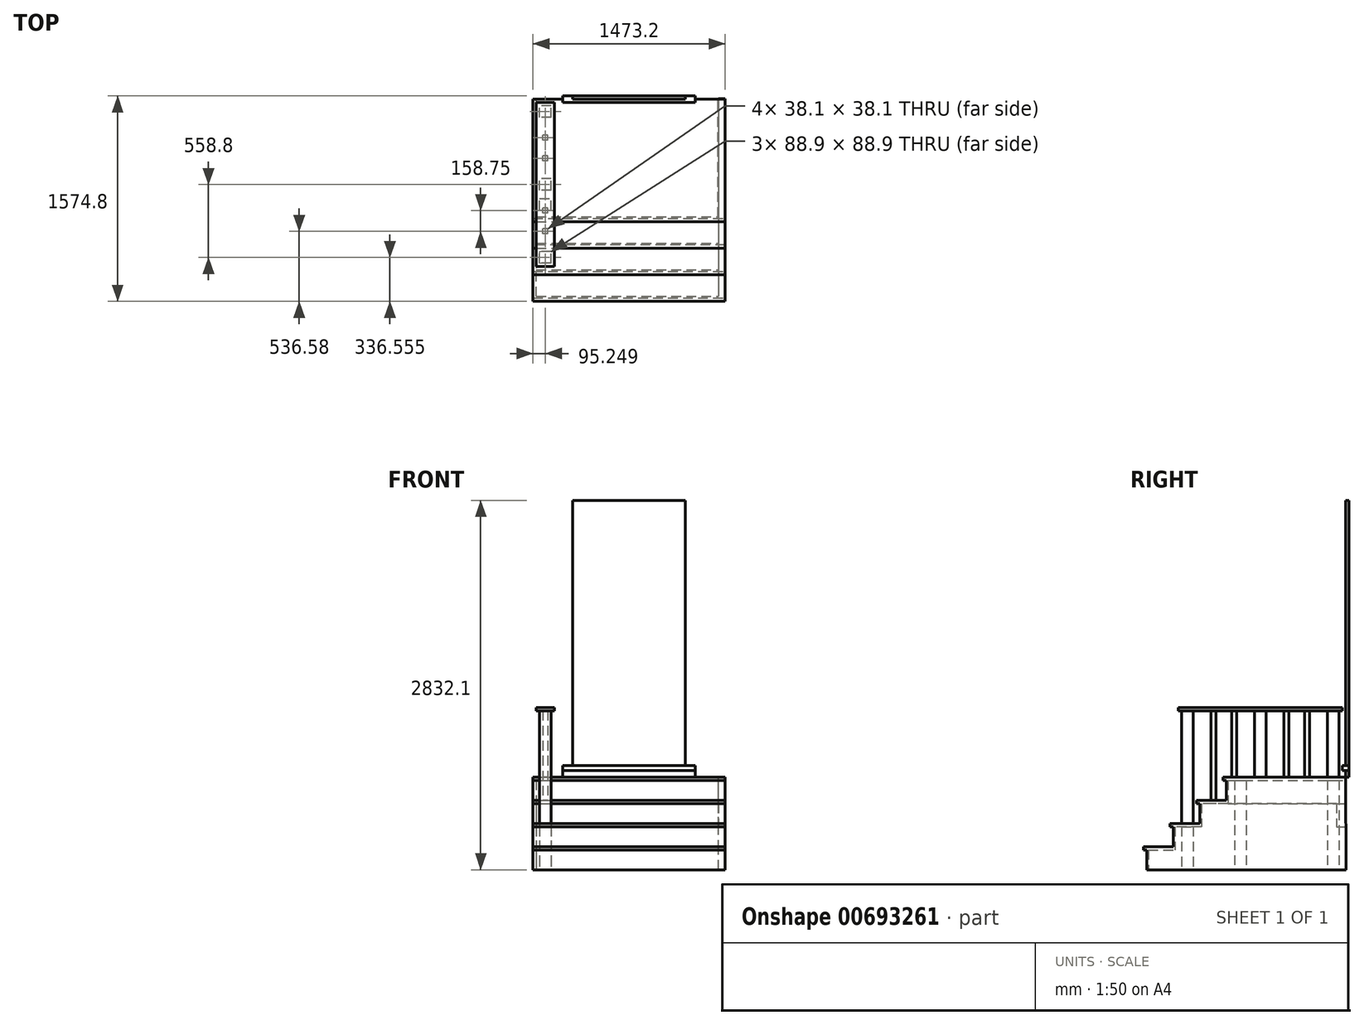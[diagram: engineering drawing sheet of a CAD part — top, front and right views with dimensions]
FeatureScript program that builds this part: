
annotation { "Feature Type Name" : "Feature", "Feature Type Description" : "" }
export const myFeature = defineFeature(function(context is Context, id is Id, definition is map)
    precondition{}
    {
        {
            var Q0;
            Q0=qCreatedBy(makeId("Top.planeOp"),FACE);
            var sketch = newSketch(context, id + "F0", { "sketchPlane" : qUnion([Q0])});
            skLineSegment(sketch, "E0", {"start": v(-1026.48, 307.92) * mm, "end": v(802.32, 307.92) * mm});
            skLineSegment(sketch, "E1", {"start": v(802.32, 307.92) * mm, "end": v(802.32, -200.08) * mm});
            skLineSegment(sketch, "E2", {"start": v(802.32, -200.08) * mm, "end": v(395.92, -606.48) * mm});
            skLineSegment(sketch, "E3", {"start": v(395.92, -606.48) * mm, "end": v(-1026.48, -606.48) * mm});
            skLineSegment(sketch, "E4", {"start": v(-1026.48, -606.48) * mm, "end": v(-1026.48, 307.92) * mm});
            skSolve(sketch);
        }
        {
            var Q0;
            Q0 = qSketchRegion(id + "F0", true);
            extrude(context, id + "F1", {"entities" : qUnion([Q0]), "depth" : 711.2 * mm, "offsetDistance" : 25.4 * mm});
        }
        {
            var Q0;
            Q0=qCreatedBy(makeId("Top.planeOp"),FACE);
            var sketch = newSketch(context, id + "F2", { "sketchPlane" : qUnion([Q0])});
            skLineSegment(sketch, "E5", {"start": v(-1026.48, -606.48) * mm, "end": v(-1026.48, -809.68) * mm});
            skLineSegment(sketch, "E6", {"start": v(-1026.48, -809.68) * mm, "end": v(480.09, -809.68) * mm});
            skLineSegment(sketch, "E7", {"start": v(480.09, -809.68) * mm, "end": v(1005.52, -284.24) * mm});
            skLineSegment(sketch, "E8", {"start": v(1005.52, -284.24) * mm, "end": v(1005.52, 307.92) * mm});
            skLineSegment(sketch, "E9", {"start": v(1005.52, 307.92) * mm, "end": v(802.32, 307.92) * mm});
            skLineSegment(sketch, "E10", {"start": v(-1026.48, -606.48) * mm, "end": v(395.92, -606.48) * mm});
            skLineSegment(sketch, "E11", {"start": v(395.92, -606.48) * mm, "end": v(802.32, -200.08) * mm});
            skLineSegment(sketch, "E12", {"start": v(802.32, -200.08) * mm, "end": v(802.32, 307.92) * mm});
            skSolve(sketch);
        }
        {
            var Q0;
            Q0 = qSketchRegion(id + "F2", true);
            extrude(context, id + "F3", {"entities" : qUnion([Q0]), "operationType" : NewBodyOperationType.ADD, "depth" : 533.4 * mm, "offsetDistance" : 25.4 * mm});
        }
        {
            var Q0;
            Q0=qCreatedBy(makeId("Top.planeOp"),FACE);
            var sketch = newSketch(context, id + "F4", { "sketchPlane" : qUnion([Q0])});
            skLineSegment(sketch, "E13", {"start": v(-1026.48, -809.68) * mm, "end": v(-1026.48, -1012.88) * mm});
            skLineSegment(sketch, "E14", {"start": v(-1026.48, -1012.88) * mm, "end": v(564.26, -1012.88) * mm});
            skLineSegment(sketch, "E15", {"start": v(564.26, -1012.88) * mm, "end": v(1208.72, -368.41) * mm});
            skLineSegment(sketch, "E16", {"start": v(1208.72, -368.41) * mm, "end": v(1208.72, 307.92) * mm});
            skLineSegment(sketch, "E17", {"start": v(1208.72, 307.92) * mm, "end": v(1005.52, 307.92) * mm});
            skLineSegment(sketch, "E18", {"start": v(1005.52, 307.92) * mm, "end": v(1005.52, -284.24) * mm});
            skLineSegment(sketch, "E19", {"start": v(1005.52, -284.24) * mm, "end": v(480.09, -809.68) * mm});
            skLineSegment(sketch, "E20", {"start": v(480.09, -809.68) * mm, "end": v(-1026.48, -809.68) * mm});
            skSolve(sketch);
        }
        {
            var Q0;
            Q0 = qSketchRegion(id + "F4", true);
            extrude(context, id + "F5", {"entities" : qUnion([Q0]), "operationType" : NewBodyOperationType.ADD, "depth" : 355.6 * mm, "offsetDistance" : 25.4 * mm});
        }
        {
            var Q0;
            Q0=qCreatedBy(makeId("Top.planeOp"),FACE);
            var sketch = newSketch(context, id + "F6", { "sketchPlane" : qUnion([Q0])});
            skLineSegment(sketch, "E21", {"start": v(-1026.48, -1012.88) * mm, "end": v(-1026.48, -1216.08) * mm});
            skLineSegment(sketch, "E22", {"start": v(-1026.48, -1216.08) * mm, "end": v(648.42, -1216.08) * mm});
            skLineSegment(sketch, "E23", {"start": v(648.42, -1216.08) * mm, "end": v(1411.92, -452.58) * mm});
            skLineSegment(sketch, "E24", {"start": v(1411.92, -452.58) * mm, "end": v(1411.92, 307.92) * mm});
            skLineSegment(sketch, "E25", {"start": v(1411.92, 307.92) * mm, "end": v(1208.72, 307.92) * mm});
            skLineSegment(sketch, "E26", {"start": v(-1026.48, -1012.88) * mm, "end": v(564.26, -1012.88) * mm});
            skLineSegment(sketch, "E27", {"start": v(564.26, -1012.88) * mm, "end": v(1208.72, -368.41) * mm});
            skLineSegment(sketch, "E28", {"start": v(1208.72, -368.41) * mm, "end": v(1208.72, 307.92) * mm});
            skSolve(sketch);
        }
        {
            var Q0;
            Q0 = qSketchRegion(id + "F6", true);
            extrude(context, id + "F7", {"entities" : qUnion([Q0]), "operationType" : NewBodyOperationType.ADD, "depth" : 177.8 * mm, "offsetDistance" : 25.4 * mm});
        }
        {
            var Q0;
            Q0=qCreatedBy(makeId("Top.planeOp"),FACE);
            var sketch = newSketch(context, id + "F8", { "sketchPlane" : qUnion([Q0])});
            skLineSegment(sketch, "E29.bottom", {"start": v(-975.68, -860.48) * mm, "end": v(-886.78, -860.48) * mm});
            skLineSegment(sketch, "E29.top", {"start": v(-975.68, -949.38) * mm, "end": v(-886.78, -949.38) * mm});
            skLineSegment(sketch, "E29.left", {"start": v(-975.68, -860.48) * mm, "end": v(-975.68, -949.38) * mm});
            skLineSegment(sketch, "E29.right", {"start": v(-886.78, -860.48) * mm, "end": v(-886.78, -949.38) * mm});
            skPoint(sketch, "E30.oppositeSnap0", {"position": v(-886.78, -904.93) * mm});
            skLineSegment(sketch, "E30.bottom", {"start": v(-975.68, 257.12) * mm, "end": v(-886.78, 257.12) * mm});
            skLineSegment(sketch, "E30.top", {"start": v(-975.68, 168.22) * mm, "end": v(-886.78, 168.22) * mm});
            skLineSegment(sketch, "E30.left", {"start": v(-975.68, 257.12) * mm, "end": v(-975.68, 168.22) * mm});
            skLineSegment(sketch, "E30.right", {"start": v(-886.78, 257.12) * mm, "end": v(-886.78, 168.22) * mm});
            skLineSegment(sketch, "E31.bottom", {"start": v(-975.68, -301.68) * mm, "end": v(-886.78, -301.68) * mm});
            skLineSegment(sketch, "E31.top", {"start": v(-975.68, -390.58) * mm, "end": v(-886.78, -390.58) * mm});
            skLineSegment(sketch, "E31.left", {"start": v(-975.68, -301.68) * mm, "end": v(-975.68, -390.58) * mm});
            skLineSegment(sketch, "E31.right", {"start": v(-886.78, -301.68) * mm, "end": v(-886.78, -390.58) * mm});
            skLineSegment(sketch, "E32.bottom", {"start": v(-950.28, 31.7) * mm, "end": v(-912.18, 31.7) * mm});
            skLineSegment(sketch, "E32.top", {"start": v(-950.28, -6.4) * mm, "end": v(-912.18, -6.4) * mm});
            skLineSegment(sketch, "E32.left", {"start": v(-950.28, 31.7) * mm, "end": v(-950.28, -6.4) * mm});
            skLineSegment(sketch, "E32.right", {"start": v(-912.18, 31.7) * mm, "end": v(-912.18, -6.4) * mm});
            skLineSegment(sketch, "E33.bottom", {"start": v(-950.28, -127.05) * mm, "end": v(-912.18, -127.05) * mm});
            skLineSegment(sketch, "E33.top", {"start": v(-950.28, -165.15) * mm, "end": v(-912.18, -165.15) * mm});
            skLineSegment(sketch, "E33.left", {"start": v(-950.28, -127.05) * mm, "end": v(-950.28, -165.15) * mm});
            skLineSegment(sketch, "E33.right", {"start": v(-912.18, -127.05) * mm, "end": v(-912.18, -165.15) * mm});
            skLineSegment(sketch, "E34.bottom", {"start": v(-950.28, -527.1) * mm, "end": v(-912.18, -527.1) * mm});
            skLineSegment(sketch, "E34.top", {"start": v(-950.28, -565.2) * mm, "end": v(-912.18, -565.2) * mm});
            skLineSegment(sketch, "E34.left", {"start": v(-950.28, -527.1) * mm, "end": v(-950.28, -565.2) * mm});
            skLineSegment(sketch, "E34.right", {"start": v(-912.18, -527.1) * mm, "end": v(-912.18, -565.2) * mm});
            skLineSegment(sketch, "E35.bottom", {"start": v(-950.28, -685.85) * mm, "end": v(-912.18, -685.85) * mm});
            skLineSegment(sketch, "E35.top", {"start": v(-950.28, -723.95) * mm, "end": v(-912.18, -723.95) * mm});
            skLineSegment(sketch, "E35.left", {"start": v(-950.28, -685.85) * mm, "end": v(-950.28, -723.95) * mm});
            skLineSegment(sketch, "E35.right", {"start": v(-912.18, -685.85) * mm, "end": v(-912.18, -723.95) * mm});
            skSolve(sketch);
        }
        {
            var Q0;
            Q0 = qSketchRegion(id + "F8", true);
            extrude(context, id + "F9", {"entities" : qUnion([Q0]), "operationType" : NewBodyOperationType.ADD, "depth" : 1219.2 * mm, "offsetDistance" : 25.4 * mm});
        }
        {
            var Q0;
            Q0=makeQuery(id+"F9.opExtrude","CAP_FACE",FACE,{"disambiguationData":[OSD([sQuery(id+"F8.wireOp",EDGE,"E30.bottom"),sQuery(id+"F8.wireOp",EDGE,"E30.top"),sQuery(id+"F8.wireOp",EDGE,"E30.left"),sQuery(id+"F8.wireOp",EDGE,"E30.right")])],"isStart":false});
            var sketch = newSketch(context, id + "F10", { "sketchPlane" : qUnion([Q0])});
            skLineSegment(sketch, "E36.bottom", {"start": v(-1000.99, 282.52) * mm, "end": v(-861.29, 282.52) * mm});
            skLineSegment(sketch, "E36.top", {"start": v(-1000.99, -974.78) * mm, "end": v(-861.29, -974.78) * mm});
            skLineSegment(sketch, "E36.left", {"start": v(-1000.99, 282.52) * mm, "end": v(-1000.99, -974.78) * mm});
            skLineSegment(sketch, "E36.right", {"start": v(-861.29, 282.52) * mm, "end": v(-861.29, -974.78) * mm});
            skSolve(sketch);
        }
        {
            var Q0;
            Q0 = qSketchRegion(id + "F10", true);
            extrude(context, id + "F11", {"entities" : qUnion([Q0]), "operationType" : NewBodyOperationType.ADD, "depth" : 25.4 * mm, "offsetDistance" : 25.4 * mm});
        }
        {
            var Q0;
            Q0=makeQuery(id+"F7.boolean.opBoolean","MERGE",FACE,{"derivedFrom":[makeQuery(id+"F5.boolean.opBoolean","MERGE",FACE,{"derivedFrom":[makeQuery(id+"F3.boolean.opBoolean","MERGE",FACE,{"derivedFrom":[makeQuery(id+"F1.opExtrude","SWEPT_FACE",FACE,{"disambiguationData":[OSD([sQuery(id+"F0.wireOp",EDGE,"E0")])]}),makeQuery(id+"F3.opExtrude","SWEPT_FACE",FACE,{"disambiguationData":[OSD([sQuery(id+"F2.wireOp",EDGE,"E9")])]})]}),makeQuery(id+"F5.opExtrude","SWEPT_FACE",FACE,{"disambiguationData":[OSD([sQuery(id+"F4.wireOp",EDGE,"E17")])]})]}),makeQuery(id+"F7.opExtrude","SWEPT_FACE",FACE,{"disambiguationData":[OSD([sQuery(id+"F6.wireOp",EDGE,"E25")])]})]});
            var sketch = newSketch(context, id + "F12", { "sketchPlane" : qUnion([Q0])});
            skLineSegment(sketch, "E37.bottom", {"start": v(-141.92, 800.1) * mm, "end": v(721.68, 800.1) * mm});
            skLineSegment(sketch, "E37.top", {"start": v(-141.92, 2832.1) * mm, "end": v(721.68, 2832.1) * mm});
            skLineSegment(sketch, "E37.left", {"start": v(-141.92, 800.1) * mm, "end": v(-141.92, 2832.1) * mm});
            skLineSegment(sketch, "E37.right", {"start": v(721.68, 800.1) * mm, "end": v(721.68, 2832.1) * mm});
            skSolve(sketch);
        }
        {
            var Q0;
            Q0 = qSketchRegion(id + "F12", true);
            extrude(context, id + "F13", {"entities" : qUnion([Q0]), "depth" : 25.4 * mm, "offsetDistance" : 25.4 * mm});
        }
        {
            var Q0;
            Q0=makeQuery(id+"F7.boolean.opBoolean","MERGE",FACE,{"derivedFrom":[makeQuery(id+"F5.boolean.opBoolean","MERGE",FACE,{"derivedFrom":[makeQuery(id+"F3.boolean.opBoolean","MERGE",FACE,{"derivedFrom":[makeQuery(id+"F1.opExtrude","SWEPT_FACE",FACE,{"disambiguationData":[OSD([sQuery(id+"F0.wireOp",EDGE,"E0")])]}),makeQuery(id+"F3.opExtrude","SWEPT_FACE",FACE,{"disambiguationData":[OSD([sQuery(id+"F2.wireOp",EDGE,"E9")])]})]}),makeQuery(id+"F5.opExtrude","SWEPT_FACE",FACE,{"disambiguationData":[OSD([sQuery(id+"F4.wireOp",EDGE,"E17")])]})]}),makeQuery(id+"F7.opExtrude","SWEPT_FACE",FACE,{"disambiguationData":[OSD([sQuery(id+"F6.wireOp",EDGE,"E25")])]})]});
            var sketch = newSketch(context, id + "F14", { "sketchPlane" : qUnion([Q0])});
            skLineSegment(sketch, "E38.bottom", {"start": v(-218.12, 800.1) * mm, "end": v(797.88, 800.1) * mm});
            skLineSegment(sketch, "E38.top", {"start": v(-218.12, 762) * mm, "end": v(797.88, 762) * mm});
            skLineSegment(sketch, "E38.left", {"start": v(-218.12, 800.1) * mm, "end": v(-218.12, 762) * mm});
            skLineSegment(sketch, "E38.right", {"start": v(797.88, 800.1) * mm, "end": v(797.88, 762) * mm});
            skSolve(sketch);
        }
        {
            var Q0;
            Q0 = qSketchRegion(id + "F14", true);
            extrude(context, id + "F15", {"entities" : qUnion([Q0]), "depth" : 25.4 * mm, "offsetDistance" : 25.4 * mm, "hasSecondDirection" : true, "secondDirectionOppositeDirection" : true, "secondDirectionDepth" : 25.4 * mm});
        }
        {
            var Q0;
            Q0=makeQuery(id+"F7.boolean.opBoolean","MERGE",FACE,{"derivedFrom":[makeQuery(id+"F5.boolean.opBoolean","MERGE",FACE,{"derivedFrom":[makeQuery(id+"F3.boolean.opBoolean","MERGE",FACE,{"derivedFrom":[makeQuery(id+"F1.opExtrude","SWEPT_FACE",FACE,{"disambiguationData":[OSD([sQuery(id+"F0.wireOp",EDGE,"E0")])]}),makeQuery(id+"F3.opExtrude","SWEPT_FACE",FACE,{"disambiguationData":[OSD([sQuery(id+"F2.wireOp",EDGE,"E9")])]})]}),makeQuery(id+"F5.opExtrude","SWEPT_FACE",FACE,{"disambiguationData":[OSD([sQuery(id+"F4.wireOp",EDGE,"E17")])]})]}),makeQuery(id+"F7.opExtrude","SWEPT_FACE",FACE,{"disambiguationData":[OSD([sQuery(id+"F6.wireOp",EDGE,"E25")])]})]});
            var sketch = newSketch(context, id + "F16", { "sketchPlane" : qUnion([Q0])});
            skLineSegment(sketch, "E39.bottom", {"start": v(-218.12, 762) * mm, "end": v(797.88, 762) * mm});
            skLineSegment(sketch, "E39.top", {"start": v(-218.12, 711.2) * mm, "end": v(797.88, 711.2) * mm});
            skLineSegment(sketch, "E39.left", {"start": v(-218.12, 762) * mm, "end": v(-218.12, 711.2) * mm});
            skLineSegment(sketch, "E39.right", {"start": v(797.88, 762) * mm, "end": v(797.88, 711.2) * mm});
            skSolve(sketch);
        }
        {
            var Q0;
            Q0 = qSketchRegion(id + "F16", true);
            extrude(context, id + "F17", {"entities" : qUnion([Q0]), "depth" : 25.4 * mm, "offsetDistance" : 25.4 * mm});
        }
        {
            var Q0;
            Q0=makeQuery(id+"F1.opExtrude","CAP_FACE",FACE,{"disambiguationData":[OSD([sQuery(id+"F0.wireOp",EDGE,"E0"),sQuery(id+"F0.wireOp",EDGE,"E1"),sQuery(id+"F0.wireOp",EDGE,"E2"),sQuery(id+"F0.wireOp",EDGE,"E3"),sQuery(id+"F0.wireOp",EDGE,"E4")])],"isStart":false});
            var sketch = newSketch(context, id + "F18", { "sketchPlane" : qUnion([Q0])});
            skLineSegment(sketch, "E40", {"start": v(-1026.48, -606.48) * mm, "end": v(-1026.48, -631.88) * mm});
            skLineSegment(sketch, "E41", {"start": v(-1026.48, -631.88) * mm, "end": v(406.44, -631.88) * mm});
            skLineSegment(sketch, "E42", {"start": v(406.44, -631.88) * mm, "end": v(827.72, -210.6) * mm});
            skLineSegment(sketch, "E43", {"start": v(827.72, -210.6) * mm, "end": v(827.72, 307.92) * mm});
            skLineSegment(sketch, "E44", {"start": v(827.72, 307.92) * mm, "end": v(802.32, 307.92) * mm});
            skLineSegment(sketch, "E45", {"start": v(802.32, 307.92) * mm, "end": v(802.32, -200.08) * mm});
            skLineSegment(sketch, "E46", {"start": v(802.32, -200.08) * mm, "end": v(395.92, -606.48) * mm});
            skLineSegment(sketch, "E47", {"start": v(395.92, -606.48) * mm, "end": v(-1026.48, -606.48) * mm});
            skSolve(sketch);
        }
        {
            var Q0;
            Q0 = qSketchRegion(id + "F18", true);
            var Q1;
            Q1=makeQuery(id+"F18.imprint","IMPRINT",FACE,{"disambiguationData":[TD([[makeQuery(id+"F18.imprint","IMPRINT",EDGE,{"derivedFrom":sQuery(id+"F18.wireOp",EDGE,"E45")}),-1.0]])]});
            extrude(context, id + "F19", {"entities" : qUnion([Q0, Q1]), "operationType" : NewBodyOperationType.ADD, "oppositeDirection" : true, "depth" : 25.4 * mm, "offsetDistance" : 25.4 * mm});
        }
        {
            var Q0;
            Q0=makeQuery(id+"F3.opExtrude","CAP_FACE",FACE,{"disambiguationData":[OSD([sQuery(id+"F2.wireOp",EDGE,"E5"),sQuery(id+"F2.wireOp",EDGE,"E6"),sQuery(id+"F2.wireOp",EDGE,"E7"),sQuery(id+"F2.wireOp",EDGE,"E8"),sQuery(id+"F2.wireOp",EDGE,"E9"),sQuery(id+"F2.wireOp",EDGE,"E10"),sQuery(id+"F2.wireOp",EDGE,"E11"),sQuery(id+"F2.wireOp",EDGE,"E12")])],"isStart":false});
            var sketch = newSketch(context, id + "F20", { "sketchPlane" : qUnion([Q0])});
            skLineSegment(sketch, "E48", {"start": v(-1026.48, -809.68) * mm, "end": v(-1026.48, -835.08) * mm});
            skLineSegment(sketch, "E49", {"start": v(-1026.48, -835.08) * mm, "end": v(490.6, -835.08) * mm});
            skLineSegment(sketch, "E50", {"start": v(490.6, -835.08) * mm, "end": v(1030.92, -294.76) * mm});
            skLineSegment(sketch, "E51", {"start": v(1030.92, -294.76) * mm, "end": v(1030.92, 308.43) * mm});
            skLineSegment(sketch, "E52", {"start": v(1030.92, 308.43) * mm, "end": v(1005.52, 307.92) * mm});
            skLineSegment(sketch, "E53", {"start": v(1005.52, 307.92) * mm, "end": v(1005.52, -284.24) * mm});
            skLineSegment(sketch, "E54", {"start": v(1005.52, -284.24) * mm, "end": v(480.09, -809.68) * mm});
            skLineSegment(sketch, "E55", {"start": v(480.09, -809.68) * mm, "end": v(-1026.48, -809.68) * mm});
            skSolve(sketch);
        }
        {
            var Q0;
            Q0 = qSketchRegion(id + "F20", true);
            extrude(context, id + "F21", {"entities" : qUnion([Q0]), "operationType" : NewBodyOperationType.ADD, "oppositeDirection" : true, "depth" : 25.4 * mm, "offsetDistance" : 25.4 * mm});
        }
        {
            var Q0;
            Q0=makeQuery(id+"F5.opExtrude","CAP_FACE",FACE,{"disambiguationData":[OSD([sQuery(id+"F4.wireOp",EDGE,"E13"),sQuery(id+"F4.wireOp",EDGE,"E14"),sQuery(id+"F4.wireOp",EDGE,"E15"),sQuery(id+"F4.wireOp",EDGE,"E16"),sQuery(id+"F4.wireOp",EDGE,"E17"),sQuery(id+"F4.wireOp",EDGE,"E18"),sQuery(id+"F4.wireOp",EDGE,"E19"),sQuery(id+"F4.wireOp",EDGE,"E20")])],"isStart":false});
            var sketch = newSketch(context, id + "F22", { "sketchPlane" : qUnion([Q0])});
            skLineSegment(sketch, "E56", {"start": v(-1026.48, -1012.88) * mm, "end": v(-1026.48, -1038.28) * mm});
            skLineSegment(sketch, "E57", {"start": v(-1026.48, -1038.28) * mm, "end": v(574.78, -1038.28) * mm});
            skLineSegment(sketch, "E58", {"start": v(574.78, -1038.28) * mm, "end": v(1234.12, -378.93) * mm});
            skLineSegment(sketch, "E59", {"start": v(1234.12, -378.93) * mm, "end": v(1234.12, 307.92) * mm});
            skLineSegment(sketch, "E60", {"start": v(1234.12, 307.92) * mm, "end": v(1208.72, 307.92) * mm});
            skLineSegment(sketch, "E61", {"start": v(1208.72, 307.92) * mm, "end": v(1208.72, -368.41) * mm});
            skLineSegment(sketch, "E62", {"start": v(1208.72, -368.41) * mm, "end": v(564.26, -1012.88) * mm});
            skLineSegment(sketch, "E63", {"start": v(564.26, -1012.88) * mm, "end": v(-1026.48, -1012.88) * mm});
            skSolve(sketch);
        }
        {
            var Q0;
            Q0 = qSketchRegion(id + "F22", true);
            extrude(context, id + "F23", {"entities" : qUnion([Q0]), "operationType" : NewBodyOperationType.ADD, "oppositeDirection" : true, "depth" : 25.4 * mm, "offsetDistance" : 25.4 * mm});
        }
        {
            var Q0;
            Q0=makeQuery(id+"F7.opExtrude","CAP_FACE",FACE,{"disambiguationData":[OSD([sQuery(id+"F6.wireOp",EDGE,"E21"),sQuery(id+"F6.wireOp",EDGE,"E22"),sQuery(id+"F6.wireOp",EDGE,"E23"),sQuery(id+"F6.wireOp",EDGE,"E24"),sQuery(id+"F6.wireOp",EDGE,"E25"),sQuery(id+"F6.wireOp",EDGE,"E26"),sQuery(id+"F6.wireOp",EDGE,"E27"),sQuery(id+"F6.wireOp",EDGE,"E28")])],"isStart":false});
            var sketch = newSketch(context, id + "F24", { "sketchPlane" : qUnion([Q0])});
            skLineSegment(sketch, "E64", {"start": v(-1026.48, -1216.08) * mm, "end": v(-1026.48, -1241.48) * mm});
            skLineSegment(sketch, "E65", {"start": v(-1026.48, -1241.48) * mm, "end": v(658.95, -1241.48) * mm});
            skLineSegment(sketch, "E66", {"start": v(658.95, -1241.48) * mm, "end": v(1439.04, -461.38) * mm});
            skLineSegment(sketch, "E67", {"start": v(1439.04, -461.38) * mm, "end": v(1437.32, 307.92) * mm});
            skLineSegment(sketch, "E68", {"start": v(1437.32, 307.92) * mm, "end": v(1411.92, 307.92) * mm});
            skLineSegment(sketch, "E69", {"start": v(1411.92, 307.92) * mm, "end": v(1411.92, -452.58) * mm});
            skLineSegment(sketch, "E70", {"start": v(1411.92, -452.58) * mm, "end": v(648.42, -1216.08) * mm});
            skLineSegment(sketch, "E71", {"start": v(648.42, -1216.08) * mm, "end": v(-1026.48, -1216.08) * mm});
            skSolve(sketch);
        }
        {
            var Q0;
            Q0 = qSketchRegion(id + "F24", true);
            extrude(context, id + "F25", {"entities" : qUnion([Q0]), "operationType" : NewBodyOperationType.ADD, "oppositeDirection" : true, "depth" : 25.4 * mm, "offsetDistance" : 25.4 * mm});
        }
        {
            var Q0;
            {var subQ0=sQuery(id+"F0.wireOp",EDGE,"E4");var subQ1=sQuery(id+"F0.wireOp",EDGE,"E3");var subQ2=sQuery(id+"F0.wireOp",EDGE,"E2");var subQ3=sQuery(id+"F0.wireOp",EDGE,"E1");var subQ4=sQuery(id+"F0.wireOp",EDGE,"E0");Q0=makeQuery(id+"F19.boolean.opBoolean","MERGE",FACE,{"derivedFrom":[makeQuery(id+"F1.opExtrude","CAP_FACE",FACE,{"disambiguationData":[OSD([subQ4,subQ3,subQ2,subQ1,subQ0])],"isStart":false}),makeQuery(id+"F19.opExtrude","CAP_FACE",FACE,{"disambiguationData":[OSD([subQ4,subQ3,subQ2,subQ1,subQ0,sQuery(id+"F8.wireOp",EDGE,"E30.bottom"),sQuery(id+"F8.wireOp",EDGE,"E30.top"),sQuery(id+"F8.wireOp",EDGE,"E30.left"),sQuery(id+"F8.wireOp",EDGE,"E30.right"),sQuery(id+"F8.wireOp",EDGE,"E31.bottom"),sQuery(id+"F8.wireOp",EDGE,"E31.top"),sQuery(id+"F8.wireOp",EDGE,"E31.left"),sQuery(id+"F8.wireOp",EDGE,"E31.right"),sQuery(id+"F8.wireOp",EDGE,"E32.bottom"),sQuery(id+"F8.wireOp",EDGE,"E32.top"),sQuery(id+"F8.wireOp",EDGE,"E32.left"),sQuery(id+"F8.wireOp",EDGE,"E32.right"),sQuery(id+"F8.wireOp",EDGE,"E33.bottom"),sQuery(id+"F8.wireOp",EDGE,"E33.top"),sQuery(id+"F8.wireOp",EDGE,"E33.left"),sQuery(id+"F8.wireOp",EDGE,"E33.right"),sQuery(id+"F8.wireOp",EDGE,"E34.bottom"),sQuery(id+"F8.wireOp",EDGE,"E34.top"),sQuery(id+"F8.wireOp",EDGE,"E34.left"),sQuery(id+"F8.wireOp",EDGE,"E34.right"),sQuery(id+"F18.wireOp",EDGE,"E40"),sQuery(id+"F18.wireOp",EDGE,"E41"),sQuery(id+"F18.wireOp",EDGE,"E42"),sQuery(id+"F18.wireOp",EDGE,"E43"),sQuery(id+"F18.wireOp",EDGE,"E44")])],"isStart":true})]});}
            var sketch = newSketch(context, id + "F26", { "sketchPlane" : qUnion([Q0])});
            skLineSegment(sketch, "E72.bottom", {"start": v(-1026.48, 206.32) * mm, "end": v(446.72, 206.32) * mm});
            skLineSegment(sketch, "E73", {"start": v(-1026.48, -492.18) * mm, "end": v(458.58, -492.18) * mm});
            skLineSegment(sketch, "E74", {"start": v(-1026.48, -352.48) * mm, "end": v(456.2, -352.48) * mm});
            skLineSegment(sketch, "E75", {"start": v(-1026.48, -212.78) * mm, "end": v(453.84, -212.78) * mm});
            skLineSegment(sketch, "E76", {"start": v(-1026.48, -73.08) * mm, "end": v(451.46, -73.08) * mm});
            skLineSegment(sketch, "E77", {"start": v(-1026.48, 66.62) * mm, "end": v(449.1, 66.62) * mm});
            skSolve(sketch);
        }
        {
            var Q0;
            Q0=makeQuery(id+"F21.boolean.opBoolean","MERGE",FACE,{"derivedFrom":[makeQuery(id+"F3.opExtrude","CAP_FACE",FACE,{"disambiguationData":[OSD([sQuery(id+"F2.wireOp",EDGE,"E5"),sQuery(id+"F2.wireOp",EDGE,"E6"),sQuery(id+"F2.wireOp",EDGE,"E7"),sQuery(id+"F2.wireOp",EDGE,"E8"),sQuery(id+"F2.wireOp",EDGE,"E9"),sQuery(id+"F2.wireOp",EDGE,"E10"),sQuery(id+"F2.wireOp",EDGE,"E11"),sQuery(id+"F2.wireOp",EDGE,"E12")])],"isStart":false}),makeQuery(id+"F21.opExtrude","CAP_FACE",FACE,{"disambiguationData":[OSD([sQuery(id+"F20.wireOp",EDGE,"E48"),sQuery(id+"F20.wireOp",EDGE,"E49"),sQuery(id+"F20.wireOp",EDGE,"E50"),sQuery(id+"F20.wireOp",EDGE,"E51"),sQuery(id+"F20.wireOp",EDGE,"E52"),sQuery(id+"F20.wireOp",EDGE,"E53"),sQuery(id+"F20.wireOp",EDGE,"E54"),sQuery(id+"F20.wireOp",EDGE,"E55")])],"isStart":true})]});
            var sketch = newSketch(context, id + "F27", { "sketchPlane" : qUnion([Q0])});
            skLineSegment(sketch, "E78", {"start": v(-1026.48, -695.38) * mm, "end": v(446.72, -695.38) * mm});
            skSolve(sketch);
        }
        {
            var Q0;
            Q0=makeQuery(id+"F23.boolean.opBoolean","MERGE",FACE,{"derivedFrom":[makeQuery(id+"F5.opExtrude","CAP_FACE",FACE,{"disambiguationData":[OSD([sQuery(id+"F4.wireOp",EDGE,"E13"),sQuery(id+"F4.wireOp",EDGE,"E14"),sQuery(id+"F4.wireOp",EDGE,"E15"),sQuery(id+"F4.wireOp",EDGE,"E16"),sQuery(id+"F4.wireOp",EDGE,"E17"),sQuery(id+"F4.wireOp",EDGE,"E18"),sQuery(id+"F4.wireOp",EDGE,"E19"),sQuery(id+"F4.wireOp",EDGE,"E20")])],"isStart":false}),makeQuery(id+"F23.opExtrude","CAP_FACE",FACE,{"disambiguationData":[OSD([sQuery(id+"F22.wireOp",EDGE,"E56"),sQuery(id+"F22.wireOp",EDGE,"E57"),sQuery(id+"F22.wireOp",EDGE,"E58"),sQuery(id+"F22.wireOp",EDGE,"E59"),sQuery(id+"F22.wireOp",EDGE,"E60"),sQuery(id+"F22.wireOp",EDGE,"E61"),sQuery(id+"F22.wireOp",EDGE,"E62"),sQuery(id+"F22.wireOp",EDGE,"E63")])],"isStart":true})]});
            var sketch = newSketch(context, id + "F28", { "sketchPlane" : qUnion([Q0])});
            skLineSegment(sketch, "E79", {"start": v(446.72, -898.58) * mm, "end": v(-1026.48, -898.58) * mm});
            skSolve(sketch);
        }
        {
            var Q0;
            Q0=makeQuery(id+"F25.boolean.opBoolean","MERGE",FACE,{"derivedFrom":[makeQuery(id+"F7.opExtrude","CAP_FACE",FACE,{"disambiguationData":[OSD([sQuery(id+"F6.wireOp",EDGE,"E21"),sQuery(id+"F6.wireOp",EDGE,"E22"),sQuery(id+"F6.wireOp",EDGE,"E23"),sQuery(id+"F6.wireOp",EDGE,"E24"),sQuery(id+"F6.wireOp",EDGE,"E25"),sQuery(id+"F6.wireOp",EDGE,"E26"),sQuery(id+"F6.wireOp",EDGE,"E27"),sQuery(id+"F6.wireOp",EDGE,"E28")])],"isStart":false}),makeQuery(id+"F25.opExtrude","CAP_FACE",FACE,{"disambiguationData":[OSD([sQuery(id+"F24.wireOp",EDGE,"E64"),sQuery(id+"F24.wireOp",EDGE,"E65"),sQuery(id+"F24.wireOp",EDGE,"E66"),sQuery(id+"F24.wireOp",EDGE,"E67"),sQuery(id+"F24.wireOp",EDGE,"E68"),sQuery(id+"F24.wireOp",EDGE,"E69"),sQuery(id+"F24.wireOp",EDGE,"E70"),sQuery(id+"F24.wireOp",EDGE,"E71")])],"isStart":true})]});
            var sketch = newSketch(context, id + "F29", { "sketchPlane" : qUnion([Q0])});
            skLineSegment(sketch, "E80", {"start": v(-1026.48, -1101.78) * mm, "end": v(446.72, -1101.78) * mm});
            skSolve(sketch);
        }
        {
            var Q0;
            Q0=makeQuery(id+"F7.boolean.opBoolean","MERGE",FACE,{"derivedFrom":[makeQuery(id+"F5.boolean.opBoolean","MERGE",FACE,{"derivedFrom":[makeQuery(id+"F3.boolean.opBoolean","MERGE",FACE,{"derivedFrom":[makeQuery(id+"F1.opExtrude","CAP_FACE",FACE,{"disambiguationData":[OSD([sQuery(id+"F0.wireOp",EDGE,"E0"),sQuery(id+"F0.wireOp",EDGE,"E1"),sQuery(id+"F0.wireOp",EDGE,"E2"),sQuery(id+"F0.wireOp",EDGE,"E3"),sQuery(id+"F0.wireOp",EDGE,"E4")])],"isStart":true}),makeQuery(id+"F3.opExtrude","CAP_FACE",FACE,{"disambiguationData":[OSD([sQuery(id+"F2.wireOp",EDGE,"E5"),sQuery(id+"F2.wireOp",EDGE,"E6"),sQuery(id+"F2.wireOp",EDGE,"E7"),sQuery(id+"F2.wireOp",EDGE,"E8"),sQuery(id+"F2.wireOp",EDGE,"E9"),sQuery(id+"F2.wireOp",EDGE,"E10"),sQuery(id+"F2.wireOp",EDGE,"E11"),sQuery(id+"F2.wireOp",EDGE,"E12")])],"isStart":true})]}),makeQuery(id+"F5.opExtrude","CAP_FACE",FACE,{"disambiguationData":[OSD([sQuery(id+"F4.wireOp",EDGE,"E13"),sQuery(id+"F4.wireOp",EDGE,"E14"),sQuery(id+"F4.wireOp",EDGE,"E15"),sQuery(id+"F4.wireOp",EDGE,"E16"),sQuery(id+"F4.wireOp",EDGE,"E17"),sQuery(id+"F4.wireOp",EDGE,"E18"),sQuery(id+"F4.wireOp",EDGE,"E19"),sQuery(id+"F4.wireOp",EDGE,"E20")])],"isStart":true})]}),makeQuery(id+"F7.opExtrude","CAP_FACE",FACE,{"disambiguationData":[OSD([sQuery(id+"F6.wireOp",EDGE,"E21"),sQuery(id+"F6.wireOp",EDGE,"E22"),sQuery(id+"F6.wireOp",EDGE,"E23"),sQuery(id+"F6.wireOp",EDGE,"E24"),sQuery(id+"F6.wireOp",EDGE,"E25"),sQuery(id+"F6.wireOp",EDGE,"E26"),sQuery(id+"F6.wireOp",EDGE,"E27"),sQuery(id+"F6.wireOp",EDGE,"E28")])],"isStart":true})]});
            var sketch = newSketch(context, id + "F30", { "sketchPlane" : qUnion([Q0])});
            skLineSegment(sketch, "E81", {"start": v(-1001.08, 593.78) * mm, "end": v(390.66, 593.78) * mm});
            skLineSegment(sketch, "E82", {"start": v(390.66, -307.92) * mm, "end": v(-1001.08, -307.92) * mm});
            skLineSegment(sketch, "E83", {"start": v(-1001.08, 593.78) * mm, "end": v(-1001.08, -307.92) * mm});
            skLineSegment(sketch, "E84", {"start": v(390.66, 593.78) * mm, "end": v(390.66, -307.92) * mm});
            skPoint(sketch, "E85.end.orphan", {"position": v(789.62, -307.92) * mm});
            skSolve(sketch);
        }
        {
            var Q0;
            Q0 = qSketchRegion(id + "F30", true);
            var Q1;
            Q1=makeQuery(id+"F19.opExtrude","CAP_FACE",FACE,{"disambiguationData":[OSD([sQuery(id+"F0.wireOp",EDGE,"E0"),sQuery(id+"F0.wireOp",EDGE,"E1"),sQuery(id+"F0.wireOp",EDGE,"E2"),sQuery(id+"F0.wireOp",EDGE,"E3"),sQuery(id+"F0.wireOp",EDGE,"E4"),sQuery(id+"F8.wireOp",EDGE,"E30.bottom"),sQuery(id+"F8.wireOp",EDGE,"E30.top"),sQuery(id+"F8.wireOp",EDGE,"E30.left"),sQuery(id+"F8.wireOp",EDGE,"E30.right"),sQuery(id+"F8.wireOp",EDGE,"E31.bottom"),sQuery(id+"F8.wireOp",EDGE,"E31.top"),sQuery(id+"F8.wireOp",EDGE,"E31.left"),sQuery(id+"F8.wireOp",EDGE,"E31.right"),sQuery(id+"F8.wireOp",EDGE,"E32.bottom"),sQuery(id+"F8.wireOp",EDGE,"E32.top"),sQuery(id+"F8.wireOp",EDGE,"E32.left"),sQuery(id+"F8.wireOp",EDGE,"E32.right"),sQuery(id+"F8.wireOp",EDGE,"E33.bottom"),sQuery(id+"F8.wireOp",EDGE,"E33.top"),sQuery(id+"F8.wireOp",EDGE,"E33.left"),sQuery(id+"F8.wireOp",EDGE,"E33.right"),sQuery(id+"F8.wireOp",EDGE,"E34.bottom"),sQuery(id+"F8.wireOp",EDGE,"E34.top"),sQuery(id+"F8.wireOp",EDGE,"E34.left"),sQuery(id+"F8.wireOp",EDGE,"E34.right"),sQuery(id+"F18.wireOp",EDGE,"E40"),sQuery(id+"F18.wireOp",EDGE,"E41"),sQuery(id+"F18.wireOp",EDGE,"E42"),sQuery(id+"F18.wireOp",EDGE,"E43"),sQuery(id+"F18.wireOp",EDGE,"E44")])],"isStart":false});
            extrude(context, id + "F31", {"entities" : qUnion([Q0]), "operationType" : NewBodyOperationType.REMOVE, "endBound" : BoundingType.UP_TO_SURFACE, "oppositeDirection" : true, "depth" : 25.4 * mm, "endBoundEntityFace" : qUnion([Q1]), "offsetDistance" : 25.4 * mm});
        }
        {
            var Q0;
            Q0=makeQuery(id+"F7.boolean.opBoolean","MERGE",FACE,{"derivedFrom":[makeQuery(id+"F5.boolean.opBoolean","MERGE",FACE,{"derivedFrom":[makeQuery(id+"F3.boolean.opBoolean","MERGE",FACE,{"derivedFrom":[makeQuery(id+"F1.opExtrude","CAP_FACE",FACE,{"disambiguationData":[OSD([sQuery(id+"F0.wireOp",EDGE,"E0"),sQuery(id+"F0.wireOp",EDGE,"E1"),sQuery(id+"F0.wireOp",EDGE,"E2"),sQuery(id+"F0.wireOp",EDGE,"E3"),sQuery(id+"F0.wireOp",EDGE,"E4")])],"isStart":true}),makeQuery(id+"F3.opExtrude","CAP_FACE",FACE,{"disambiguationData":[OSD([sQuery(id+"F2.wireOp",EDGE,"E5"),sQuery(id+"F2.wireOp",EDGE,"E6"),sQuery(id+"F2.wireOp",EDGE,"E7"),sQuery(id+"F2.wireOp",EDGE,"E8"),sQuery(id+"F2.wireOp",EDGE,"E9"),sQuery(id+"F2.wireOp",EDGE,"E10"),sQuery(id+"F2.wireOp",EDGE,"E11"),sQuery(id+"F2.wireOp",EDGE,"E12")])],"isStart":true})]}),makeQuery(id+"F5.opExtrude","CAP_FACE",FACE,{"disambiguationData":[OSD([sQuery(id+"F4.wireOp",EDGE,"E13"),sQuery(id+"F4.wireOp",EDGE,"E14"),sQuery(id+"F4.wireOp",EDGE,"E15"),sQuery(id+"F4.wireOp",EDGE,"E16"),sQuery(id+"F4.wireOp",EDGE,"E17"),sQuery(id+"F4.wireOp",EDGE,"E18"),sQuery(id+"F4.wireOp",EDGE,"E19"),sQuery(id+"F4.wireOp",EDGE,"E20")])],"isStart":true})]}),makeQuery(id+"F7.opExtrude","CAP_FACE",FACE,{"disambiguationData":[OSD([sQuery(id+"F6.wireOp",EDGE,"E21"),sQuery(id+"F6.wireOp",EDGE,"E22"),sQuery(id+"F6.wireOp",EDGE,"E23"),sQuery(id+"F6.wireOp",EDGE,"E24"),sQuery(id+"F6.wireOp",EDGE,"E25"),sQuery(id+"F6.wireOp",EDGE,"E26"),sQuery(id+"F6.wireOp",EDGE,"E27"),sQuery(id+"F6.wireOp",EDGE,"E28")])],"isStart":true})]});
            var sketch = newSketch(context, id + "F32", { "sketchPlane" : qUnion([Q0])});
            skLineSegment(sketch, "E86", {"start": v(-1001.08, 796.98) * mm, "end": v(474.83, 796.98) * mm});
            skLineSegment(sketch, "E87", {"start": v(390.66, -307.92) * mm, "end": v(-1001.08, -307.92) * mm});
            skLineSegment(sketch, "E88", {"start": v(-1001.08, -307.92) * mm, "end": v(-1001.08, 796.98) * mm});
            skPoint(sketch, "E89.orphan", {"position": v(-1026.48, -307.92) * mm});
            skPoint(sketch, "E90.orphan", {"position": v(-1026.48, 796.98) * mm});
            skLineSegment(sketch, "E91", {"start": v(474.83, 796.98) * mm, "end": v(390.66, -307.92) * mm});
            skSolve(sketch);
        }
        {
            var Q0;
            Q0 = qSketchRegion(id + "F32", true);
            var Q1;
            Q1=makeQuery(id+"F21.opExtrude","CAP_FACE",FACE,{"disambiguationData":[OSD([sQuery(id+"F20.wireOp",EDGE,"E48"),sQuery(id+"F20.wireOp",EDGE,"E49"),sQuery(id+"F20.wireOp",EDGE,"E50"),sQuery(id+"F20.wireOp",EDGE,"E51"),sQuery(id+"F20.wireOp",EDGE,"E52"),sQuery(id+"F20.wireOp",EDGE,"E53"),sQuery(id+"F20.wireOp",EDGE,"E54"),sQuery(id+"F20.wireOp",EDGE,"E55")])],"isStart":false});
            extrude(context, id + "F33", {"entities" : qUnion([Q0]), "operationType" : NewBodyOperationType.REMOVE, "endBound" : BoundingType.UP_TO_SURFACE, "oppositeDirection" : true, "depth" : 25.4 * mm, "endBoundEntityFace" : qUnion([Q1]), "offsetDistance" : 25.4 * mm});
        }
        {
            var Q0;
            Q0=makeQuery(id+"F7.boolean.opBoolean","MERGE",FACE,{"derivedFrom":[makeQuery(id+"F5.boolean.opBoolean","MERGE",FACE,{"derivedFrom":[makeQuery(id+"F3.boolean.opBoolean","MERGE",FACE,{"derivedFrom":[makeQuery(id+"F1.opExtrude","CAP_FACE",FACE,{"disambiguationData":[OSD([sQuery(id+"F0.wireOp",EDGE,"E0"),sQuery(id+"F0.wireOp",EDGE,"E1"),sQuery(id+"F0.wireOp",EDGE,"E2"),sQuery(id+"F0.wireOp",EDGE,"E3"),sQuery(id+"F0.wireOp",EDGE,"E4")])],"isStart":true}),makeQuery(id+"F3.opExtrude","CAP_FACE",FACE,{"disambiguationData":[OSD([sQuery(id+"F2.wireOp",EDGE,"E5"),sQuery(id+"F2.wireOp",EDGE,"E6"),sQuery(id+"F2.wireOp",EDGE,"E7"),sQuery(id+"F2.wireOp",EDGE,"E8"),sQuery(id+"F2.wireOp",EDGE,"E9"),sQuery(id+"F2.wireOp",EDGE,"E10"),sQuery(id+"F2.wireOp",EDGE,"E11"),sQuery(id+"F2.wireOp",EDGE,"E12")])],"isStart":true})]}),makeQuery(id+"F5.opExtrude","CAP_FACE",FACE,{"disambiguationData":[OSD([sQuery(id+"F4.wireOp",EDGE,"E13"),sQuery(id+"F4.wireOp",EDGE,"E14"),sQuery(id+"F4.wireOp",EDGE,"E15"),sQuery(id+"F4.wireOp",EDGE,"E16"),sQuery(id+"F4.wireOp",EDGE,"E17"),sQuery(id+"F4.wireOp",EDGE,"E18"),sQuery(id+"F4.wireOp",EDGE,"E19"),sQuery(id+"F4.wireOp",EDGE,"E20")])],"isStart":true})]}),makeQuery(id+"F7.opExtrude","CAP_FACE",FACE,{"disambiguationData":[OSD([sQuery(id+"F6.wireOp",EDGE,"E21"),sQuery(id+"F6.wireOp",EDGE,"E22"),sQuery(id+"F6.wireOp",EDGE,"E23"),sQuery(id+"F6.wireOp",EDGE,"E24"),sQuery(id+"F6.wireOp",EDGE,"E25"),sQuery(id+"F6.wireOp",EDGE,"E26"),sQuery(id+"F6.wireOp",EDGE,"E27"),sQuery(id+"F6.wireOp",EDGE,"E28")])],"isStart":true})]});
            var sketch = newSketch(context, id + "F34", { "sketchPlane" : qUnion([Q0])});
            skLineSegment(sketch, "E92", {"start": v(-1001.08, 1000.18) * mm, "end": v(421.32, 1000.18) * mm});
            skLineSegment(sketch, "E93", {"start": v(421.32, -307.92) * mm, "end": v(-1001.08, -307.92) * mm});
            skLineSegment(sketch, "E94", {"start": v(-1001.08, -307.92) * mm, "end": v(-1001.08, 1000.18) * mm});
            skPoint(sketch, "E95.orphan", {"position": v(-1026.48, -307.92) * mm});
            skLineSegment(sketch, "E96", {"start": v(421.32, 1000.18) * mm, "end": v(421.32, -307.92) * mm});
            skSolve(sketch);
        }
        {
            var Q0;
            Q0 = qSketchRegion(id + "F34", true);
            var Q1;
            Q1=makeQuery(id+"F23.opExtrude","CAP_FACE",FACE,{"disambiguationData":[OSD([sQuery(id+"F22.wireOp",EDGE,"E56"),sQuery(id+"F22.wireOp",EDGE,"E57"),sQuery(id+"F22.wireOp",EDGE,"E58"),sQuery(id+"F22.wireOp",EDGE,"E59"),sQuery(id+"F22.wireOp",EDGE,"E60"),sQuery(id+"F22.wireOp",EDGE,"E61"),sQuery(id+"F22.wireOp",EDGE,"E62"),sQuery(id+"F22.wireOp",EDGE,"E63")])],"isStart":false});
            extrude(context, id + "F35", {"entities" : qUnion([Q0]), "operationType" : NewBodyOperationType.REMOVE, "endBound" : BoundingType.UP_TO_SURFACE, "oppositeDirection" : true, "depth" : 25.4 * mm, "endBoundEntityFace" : qUnion([Q1]), "offsetDistance" : 25.4 * mm});
        }
        {
            var Q0;
            Q0=makeQuery(id+"F7.boolean.opBoolean","MERGE",FACE,{"derivedFrom":[makeQuery(id+"F5.boolean.opBoolean","MERGE",FACE,{"derivedFrom":[makeQuery(id+"F3.boolean.opBoolean","MERGE",FACE,{"derivedFrom":[makeQuery(id+"F1.opExtrude","CAP_FACE",FACE,{"disambiguationData":[OSD([sQuery(id+"F0.wireOp",EDGE,"E0"),sQuery(id+"F0.wireOp",EDGE,"E1"),sQuery(id+"F0.wireOp",EDGE,"E2"),sQuery(id+"F0.wireOp",EDGE,"E3"),sQuery(id+"F0.wireOp",EDGE,"E4")])],"isStart":true}),makeQuery(id+"F3.opExtrude","CAP_FACE",FACE,{"disambiguationData":[OSD([sQuery(id+"F2.wireOp",EDGE,"E5"),sQuery(id+"F2.wireOp",EDGE,"E6"),sQuery(id+"F2.wireOp",EDGE,"E7"),sQuery(id+"F2.wireOp",EDGE,"E8"),sQuery(id+"F2.wireOp",EDGE,"E9"),sQuery(id+"F2.wireOp",EDGE,"E10"),sQuery(id+"F2.wireOp",EDGE,"E11"),sQuery(id+"F2.wireOp",EDGE,"E12")])],"isStart":true})]}),makeQuery(id+"F5.opExtrude","CAP_FACE",FACE,{"disambiguationData":[OSD([sQuery(id+"F4.wireOp",EDGE,"E13"),sQuery(id+"F4.wireOp",EDGE,"E14"),sQuery(id+"F4.wireOp",EDGE,"E15"),sQuery(id+"F4.wireOp",EDGE,"E16"),sQuery(id+"F4.wireOp",EDGE,"E17"),sQuery(id+"F4.wireOp",EDGE,"E18"),sQuery(id+"F4.wireOp",EDGE,"E19"),sQuery(id+"F4.wireOp",EDGE,"E20")])],"isStart":true})]}),makeQuery(id+"F7.opExtrude","CAP_FACE",FACE,{"disambiguationData":[OSD([sQuery(id+"F6.wireOp",EDGE,"E21"),sQuery(id+"F6.wireOp",EDGE,"E22"),sQuery(id+"F6.wireOp",EDGE,"E23"),sQuery(id+"F6.wireOp",EDGE,"E24"),sQuery(id+"F6.wireOp",EDGE,"E25"),sQuery(id+"F6.wireOp",EDGE,"E26"),sQuery(id+"F6.wireOp",EDGE,"E27"),sQuery(id+"F6.wireOp",EDGE,"E28")])],"isStart":true})]});
            var sketch = newSketch(context, id + "F36", { "sketchPlane" : qUnion([Q0])});
            skLineSegment(sketch, "E97", {"start": v(-1001.08, 1203.38) * mm, "end": v(637.87, 1203.38) * mm});
            skLineSegment(sketch, "E98", {"start": v(637.87, 1203.38) * mm, "end": v(648.42, 1192.82) * mm});
            skLineSegment(sketch, "E99", {"start": v(648.42, -307.92) * mm, "end": v(-1001.08, -307.92) * mm});
            skLineSegment(sketch, "E100", {"start": v(-1001.08, -307.92) * mm, "end": v(-1001.08, 1203.38) * mm});
            skPoint(sketch, "E101.orphan", {"position": v(-1026.48, -307.92) * mm});
            skLineSegment(sketch, "E102", {"start": v(648.42, 1216.08) * mm, "end": v(648.42, -307.92) * mm});
            skPoint(sketch, "E103.end.orphan", {"position": v(1399.22, -307.92) * mm});
            skSolve(sketch);
        }
        {
            var Q0;
            Q0 = qSketchRegion(id + "F36", true);
            var Q1;
            Q1=makeQuery(id+"F25.opExtrude","CAP_FACE",FACE,{"disambiguationData":[OSD([sQuery(id+"F24.wireOp",EDGE,"E64"),sQuery(id+"F24.wireOp",EDGE,"E65"),sQuery(id+"F24.wireOp",EDGE,"E66"),sQuery(id+"F24.wireOp",EDGE,"E67"),sQuery(id+"F24.wireOp",EDGE,"E68"),sQuery(id+"F24.wireOp",EDGE,"E69"),sQuery(id+"F24.wireOp",EDGE,"E70"),sQuery(id+"F24.wireOp",EDGE,"E71")])],"isStart":false});
            extrude(context, id + "F37", {"entities" : qUnion([Q0]), "operationType" : NewBodyOperationType.REMOVE, "endBound" : BoundingType.UP_TO_SURFACE, "oppositeDirection" : true, "depth" : 25.4 * mm, "endBoundEntityFace" : qUnion([Q1]), "offsetDistance" : 25.4 * mm});
        }
        {
            var Q0;
            Q0=makeQuery(id+"F7.boolean.opBoolean","MERGE",FACE,{"derivedFrom":[makeQuery(id+"F5.boolean.opBoolean","MERGE",FACE,{"derivedFrom":[makeQuery(id+"F3.boolean.opBoolean","MERGE",FACE,{"derivedFrom":[makeQuery(id+"F1.opExtrude","CAP_FACE",FACE,{"disambiguationData":[OSD([sQuery(id+"F0.wireOp",EDGE,"E0"),sQuery(id+"F0.wireOp",EDGE,"E1"),sQuery(id+"F0.wireOp",EDGE,"E2"),sQuery(id+"F0.wireOp",EDGE,"E3"),sQuery(id+"F0.wireOp",EDGE,"E4")])],"isStart":true}),makeQuery(id+"F3.opExtrude","CAP_FACE",FACE,{"disambiguationData":[OSD([sQuery(id+"F2.wireOp",EDGE,"E5"),sQuery(id+"F2.wireOp",EDGE,"E6"),sQuery(id+"F2.wireOp",EDGE,"E7"),sQuery(id+"F2.wireOp",EDGE,"E8"),sQuery(id+"F2.wireOp",EDGE,"E9"),sQuery(id+"F2.wireOp",EDGE,"E10"),sQuery(id+"F2.wireOp",EDGE,"E11"),sQuery(id+"F2.wireOp",EDGE,"E12")])],"isStart":true})]}),makeQuery(id+"F5.opExtrude","CAP_FACE",FACE,{"disambiguationData":[OSD([sQuery(id+"F4.wireOp",EDGE,"E13"),sQuery(id+"F4.wireOp",EDGE,"E14"),sQuery(id+"F4.wireOp",EDGE,"E15"),sQuery(id+"F4.wireOp",EDGE,"E16"),sQuery(id+"F4.wireOp",EDGE,"E17"),sQuery(id+"F4.wireOp",EDGE,"E18"),sQuery(id+"F4.wireOp",EDGE,"E19"),sQuery(id+"F4.wireOp",EDGE,"E20")])],"isStart":true})]}),makeQuery(id+"F7.opExtrude","CAP_FACE",FACE,{"disambiguationData":[OSD([sQuery(id+"F6.wireOp",EDGE,"E21"),sQuery(id+"F6.wireOp",EDGE,"E22"),sQuery(id+"F6.wireOp",EDGE,"E23"),sQuery(id+"F6.wireOp",EDGE,"E24"),sQuery(id+"F6.wireOp",EDGE,"E25"),sQuery(id+"F6.wireOp",EDGE,"E26"),sQuery(id+"F6.wireOp",EDGE,"E27"),sQuery(id+"F6.wireOp",EDGE,"E28")])],"isStart":true})]});
            var sketch = newSketch(context, id + "F38", { "sketchPlane" : qUnion([Q0])});
            skLineSegment(sketch, "E104.bottom", {"start": v(-975.68, -168.22) * mm, "end": v(-886.78, -168.22) * mm});
            skLineSegment(sketch, "E104.top", {"start": v(-975.68, -257.12) * mm, "end": v(-886.78, -257.12) * mm});
            skLineSegment(sketch, "E104.left", {"start": v(-975.68, -168.22) * mm, "end": v(-975.68, -257.12) * mm});
            skLineSegment(sketch, "E104.right", {"start": v(-886.78, -168.22) * mm, "end": v(-886.78, -257.12) * mm});
            skLineSegment(sketch, "E105.bottom", {"start": v(-975.68, 542.98) * mm, "end": v(-886.78, 542.98) * mm});
            skLineSegment(sketch, "E105.top", {"start": v(-975.68, 454.08) * mm, "end": v(-886.78, 454.08) * mm});
            skLineSegment(sketch, "E105.left", {"start": v(-975.68, 542.98) * mm, "end": v(-975.68, 454.08) * mm});
            skLineSegment(sketch, "E105.right", {"start": v(-886.78, 542.98) * mm, "end": v(-886.78, 454.08) * mm});
            skLineSegment(sketch, "E106.bottom", {"start": v(-975.68, 949.38) * mm, "end": v(-886.78, 949.38) * mm});
            skLineSegment(sketch, "E106.top", {"start": v(-975.68, 860.48) * mm, "end": v(-886.78, 860.48) * mm});
            skLineSegment(sketch, "E106.left", {"start": v(-975.68, 949.38) * mm, "end": v(-975.68, 860.48) * mm});
            skLineSegment(sketch, "E106.right", {"start": v(-886.78, 949.38) * mm, "end": v(-886.78, 860.48) * mm});
            skSolve(sketch);
        }
        {
            var Q0;
            Q0 = qSketchRegion(id + "F38", true);
            var Q1;
            Q1=makeQuery(id+"F1.opExtrude","SWEPT_BODY",BODY,{"disambiguationData":[OSD([sQuery(id+"F0.wireOp",EDGE,"E0"),sQuery(id+"F0.wireOp",EDGE,"E1"),sQuery(id+"F0.wireOp",EDGE,"E2"),sQuery(id+"F0.wireOp",EDGE,"E3"),sQuery(id+"F0.wireOp",EDGE,"E4")])]});
            extrude(context, id + "F39", {"entities" : qUnion([Q0]), "operationType" : NewBodyOperationType.ADD, "endBound" : BoundingType.UP_TO_BODY, "oppositeDirection" : true, "depth" : 25.4 * mm, "endBoundEntityBody" : qUnion([Q1]), "offsetDistance" : 25.4 * mm});
        }
        {
            var Q0;
            {var subQ9=makeQuery(id+"F19.opExtrude","CAP_EDGE",EDGE,{"disambiguationData":[OSD([sQuery(id+"F18.wireOp",EDGE,"E41")])],"isStart":true});Q0=makeQuery(id+"F26.imprint","IMPRINT",FACE,{"disambiguationData":[TD([[makeQuery(id+"F26.imprint","IMPRINT",EDGE,{"derivedFrom":subQ9}),1.0]])]});}
            var sketch = newSketch(context, id + "F40", { "sketchPlane" : qUnion([Q0])});
            skLineSegment(sketch, "E107.bottom", {"start": v(395.92, 400.84) * mm, "end": v(1667.94, 400.84) * mm});
            skLineSegment(sketch, "E107.top", {"start": v(395.92, -1345.97) * mm, "end": v(1667.94, -1345.97) * mm});
            skLineSegment(sketch, "E107.left", {"start": v(395.92, 400.84) * mm, "end": v(395.92, -1345.97) * mm});
            skLineSegment(sketch, "E107.right", {"start": v(1667.94, 400.84) * mm, "end": v(1667.94, -1345.97) * mm});
            skSolve(sketch);
        }
        {
            var Q0;
            Q0 = qSketchRegion(id + "F40", true);
            extrude(context, id + "F41", {"entities" : qUnion([Q0]), "operationType" : NewBodyOperationType.REMOVE, "oppositeDirection" : true, "depth" : 2006.6 * mm, "offsetDistance" : 25.4 * mm});
        }
        {
            var Q0;
            Q0=makeQuery(id+"F41.boolean.opBoolean","COPY",FACE,{"derivedFrom":makeQuery(id+"F41.opExtrude","SWEPT_FACE",FACE,{"disambiguationData":[OSD([sQuery(id+"F40.wireOp",EDGE,"E107.left")])]})});
            var sketch = newSketch(context, id + "F42", { "sketchPlane" : qUnion([Q0])});
            skLineSegment(sketch, "E108", {"start": v(307.92, 711.2) * mm, "end": v(-631.88, 711.2) * mm});
            skLineSegment(sketch, "E109", {"start": v(-631.88, 711.2) * mm, "end": v(-631.88, 685.8) * mm});
            skLineSegment(sketch, "E110", {"start": v(-631.88, 685.8) * mm, "end": v(-606.48, 685.8) * mm});
            skLineSegment(sketch, "E111", {"start": v(-606.48, 685.8) * mm, "end": v(-606.48, 533.4) * mm});
            skLineSegment(sketch, "E112", {"start": v(-606.48, 533.4) * mm, "end": v(-835.08, 533.4) * mm});
            skLineSegment(sketch, "E113", {"start": v(-835.08, 533.4) * mm, "end": v(-835.08, 508) * mm});
            skLineSegment(sketch, "E114", {"start": v(-835.08, 508) * mm, "end": v(-809.68, 508) * mm});
            skLineSegment(sketch, "E115", {"start": v(-809.68, 508) * mm, "end": v(-809.68, 355.6) * mm});
            skLineSegment(sketch, "E116", {"start": v(-809.68, 355.6) * mm, "end": v(-1038.28, 355.6) * mm});
            skLineSegment(sketch, "E117", {"start": v(-1038.28, 355.6) * mm, "end": v(-1038.28, 330.2) * mm});
            skLineSegment(sketch, "E118", {"start": v(-1038.28, 330.2) * mm, "end": v(-1012.88, 330.2) * mm});
            skLineSegment(sketch, "E119", {"start": v(-1012.88, 330.2) * mm, "end": v(-1012.88, 177.8) * mm});
            skLineSegment(sketch, "E120", {"start": v(-1012.88, 177.8) * mm, "end": v(-1241.48, 177.8) * mm});
            skLineSegment(sketch, "E121", {"start": v(-1241.48, 177.8) * mm, "end": v(-1241.48, 152.4) * mm});
            skLineSegment(sketch, "E122", {"start": v(-1241.48, 152.4) * mm, "end": v(-1216.08, 152.4) * mm});
            skLineSegment(sketch, "E123", {"start": v(-1216.08, 152.4) * mm, "end": v(-1216.08, 0) * mm});
            skLineSegment(sketch, "E124", {"start": v(-1216.08, 0) * mm, "end": v(311.27, 0) * mm});
            skLineSegment(sketch, "E125", {"start": v(311.27, 0) * mm, "end": v(307.92, 711.2) * mm});
            skSolve(sketch);
        }
        {
            var Q0;
            Q0 = qSketchRegion(id + "F42", true);
            extrude(context, id + "F43", {"entities" : qUnion([Q0]), "operationType" : NewBodyOperationType.ADD, "depth" : 50.8 * mm, "offsetDistance" : 25.4 * mm});
        }
    });
